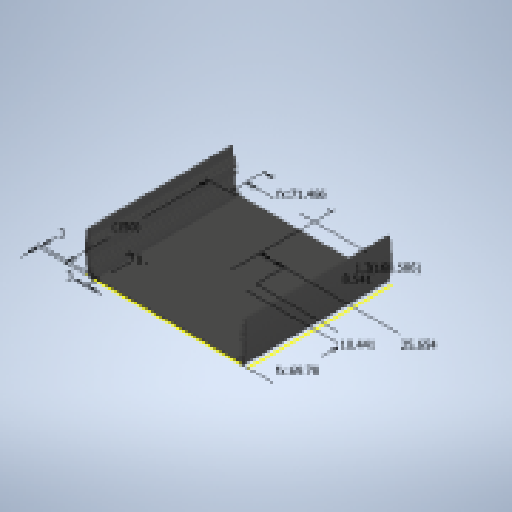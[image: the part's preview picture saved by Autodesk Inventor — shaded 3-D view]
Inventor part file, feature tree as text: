
AUTODESK INVENTOR PART (.ipt)
format: ipt  version: 2024.2 (Build 282272000, 272)  size: 577,536 bytes
history: native  units: mm
features: other x5, sketch x1, reference x1
ambient origin geometry x8: Origin, YZ Plane, XZ Plane, XY Plane, X Axis, Y Axis, Z Axis, Center Point
bodies: Solid1 (feature_tree), Volumenkörper1 (feature_tree)
feature tree (7):
  sketch  "Sketch1"  dims[d0=0.0mm d1=3.0mm d2=3.0mm d3=10.440924mm d4=69.779538mm d5=150.0mm d6=25.654376mm d7=168.586321mm d8=71.465973mm d9=8.540917mm d10=1.3mm]
  reference  "Reference1"
  other  "<userpath>\Documents\GitHub\REACH-Hardware\CAD\InventorProject\Main_Assembly_GBit.iam"
  other  "Main_Assembly_GBit.iam"
  other  "Front_Panel_Assembly_10Gbit:1"
  other  "Front_Pane_Basel_Assembly:1"
  other  "DI 1600-6000:1"
